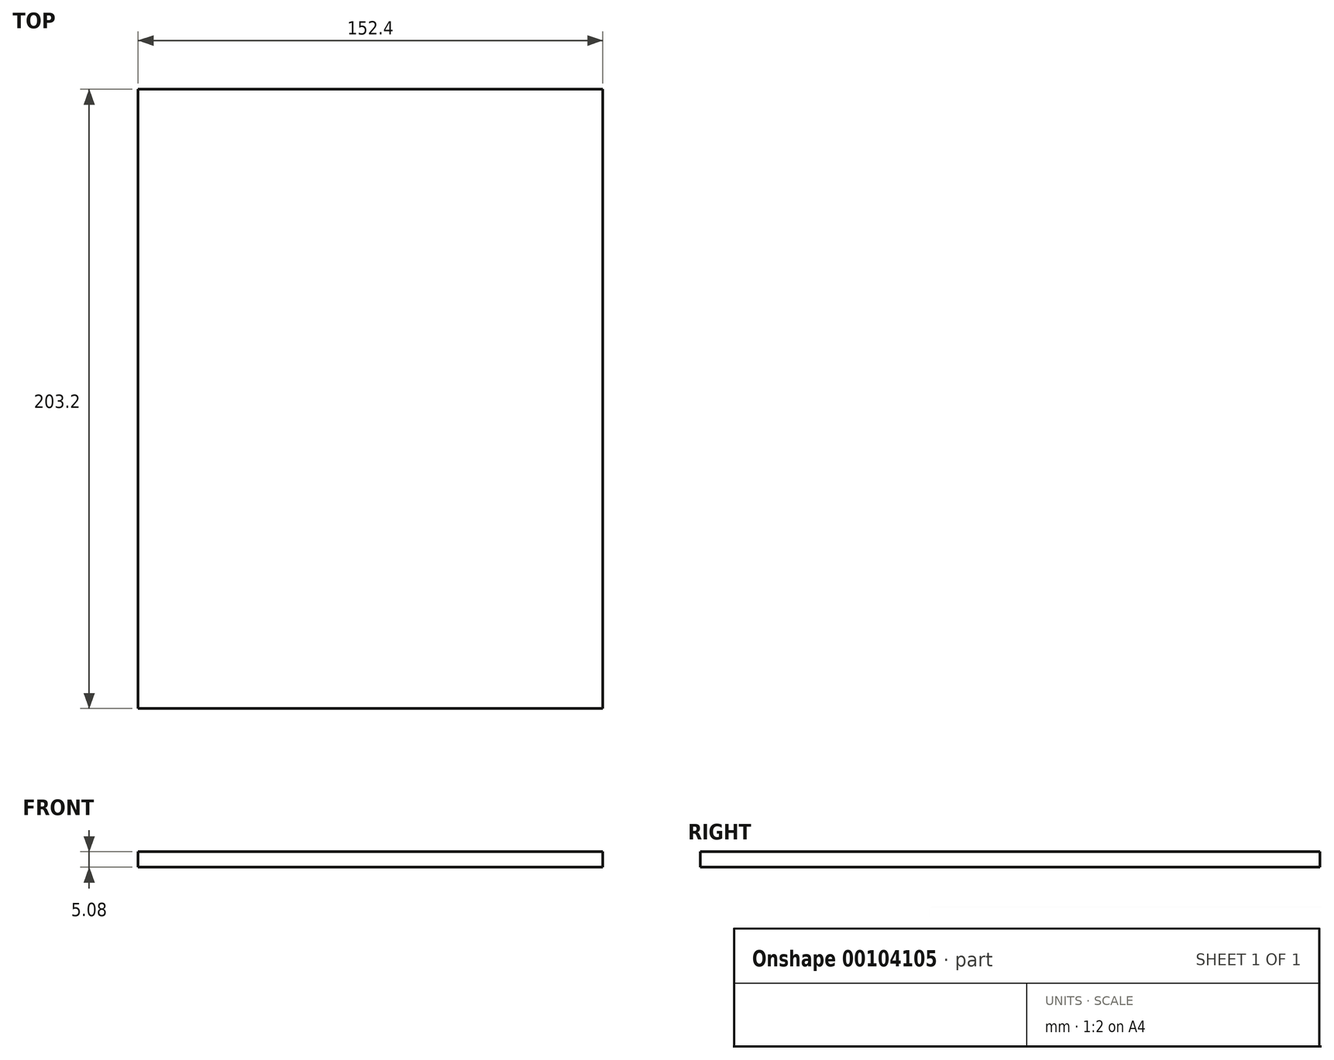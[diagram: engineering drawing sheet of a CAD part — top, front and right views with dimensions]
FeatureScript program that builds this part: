
annotation { "Feature Type Name" : "Feature", "Feature Type Description" : "" }
export const myFeature = defineFeature(function(context is Context, id is Id, definition is map)
    precondition{}
    {
        {
            var Q0;
            Q0=qCreatedBy(makeId("Front.planeOp"),FACE);
            var sketch = newSketch(context, id + "F0", { "sketchPlane" : qUnion([Q0])});
            skLineSegment(sketch, "E0.bottom", {"start": v(2.66, 4.68) * mm, "end": v(155.06, 4.68) * mm});
            skLineSegment(sketch, "E0.top", {"start": v(2.66, -0.4) * mm, "end": v(155.06, -0.4) * mm});
            skLineSegment(sketch, "E0.left", {"start": v(2.66, 4.68) * mm, "end": v(2.66, -0.4) * mm});
            skLineSegment(sketch, "E0.right", {"start": v(155.06, 4.68) * mm, "end": v(155.06, -0.4) * mm});
            skSolve(sketch);
        }
        {
            var Q0;
            Q0 = qSketchRegion(id + "F0", true);
            extrude(context, id + "F1", {"entities" : qUnion([Q0]), "depth" : 203.2 * mm});
        }
    });
